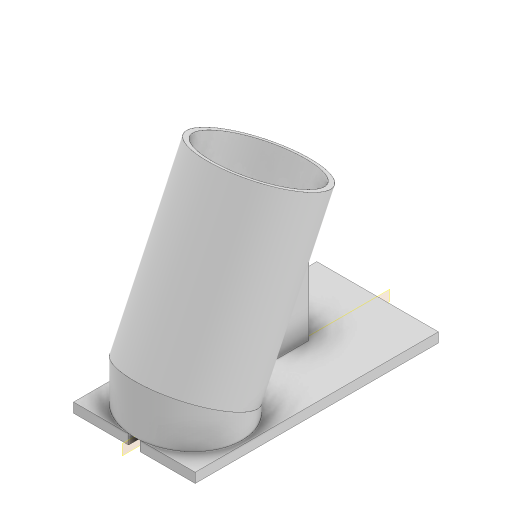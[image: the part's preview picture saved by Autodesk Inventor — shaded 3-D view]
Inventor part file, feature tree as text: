
AUTODESK INVENTOR PART (.ipt)
format: ipt  version: 2024 (Build 280153000, 153)  size: 174,592 bytes
history: native  units: mm
features: sketch x6, extrude x5, projected_geometry x2, plane x1, revolve x1
ambient origin geometry x8: Origin, YZ Plane, XZ Plane, XY Plane, X Axis, Y Axis, Z Axis, Center Point
bodies: Solid1 (feature_tree)
feature tree (15):
  extrude  "Extrusion1"  Depth=100.0mm
  plane  "Work Plane1"
  revolve  "Revolution1"  [1 undecoded]
  extrude  "Extrusion2"  Depth=46.5mm
  extrude  "Extrusion3"  Depth=2.0mm
  extrude  "Extrusion4"  Depth=70.0mm
  extrude  "Extrusion5"  Depth=27.75mm TaperAngle=0.0deg
  sketch  "Sketch1"  dims[d0=50.0mm d1=100.0mm]
  sketch  "Sketch2"  dims[d2=4.0mm d3=0.0mm d4=-25.0mm]
  sketch  "Sketch3"  dims[d5=20.0mm d6=46.5mm]
  projected_geometry  "Projected Loop1"
  sketch  "Sketch4"  dims[d7=2.0mm d8=2.0mm]
  projected_geometry  "Projected Loop2"
  sketch  "Sketch5"  dims[d9=90.0deg d10=70.0mm]
  sketch  "Sketch7"  dims[d11=4.0mm d12=0.0mm d13=27.75mm d14=0.0mm d15=4.0mm d16=0.0mm d17=3.0mm d18=4.0mm d19=0.0mm]
note: 1 required parameter value undecoded (feature->parameter linkage not recoverable at this tier; creation-order binding heuristic only, values carry confidence <= 0.55)
